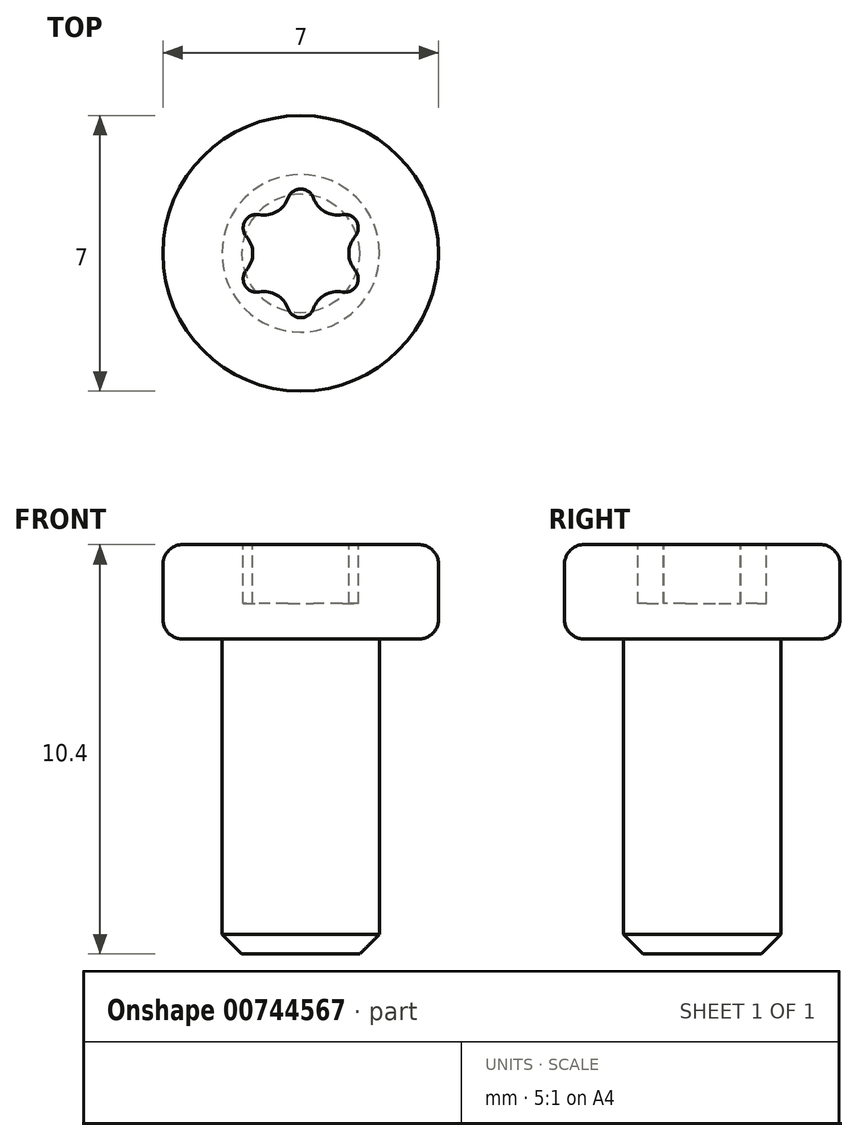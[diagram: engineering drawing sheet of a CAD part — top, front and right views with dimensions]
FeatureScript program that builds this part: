
annotation { "Feature Type Name" : "Feature", "Feature Type Description" : "" }
export const myFeature = defineFeature(function(context is Context, id is Id, definition is map)
    precondition{}
    {
        {
            var Q0;
            Q0=qCreatedBy(makeId("Top.planeOp"),FACE);
            var sketch = newSketch(context, id + "F0", { "sketchPlane" : qUnion([Q0])});
            skCircle(sketch, "E0", {"center": v(0, 0) * mm, "radius": 2 * mm});
            skSolve(sketch);
        }
        {
            var Q0;
            Q0=makeQuery(id+"F0.imprint","IMPRINT",FACE,{"disambiguationData":[TD([[makeQuery(id+"F0.imprint","IMPRINT",EDGE,{"derivedFrom":sQuery(id+"F0.wireOp",EDGE,"E0")}),1.0]])]});
            extrude(context, id + "F1", {"entities" : qUnion([Q0]), "depth" : 8 * mm, "offsetDistance" : 25 * mm});
        }
        {
            var Q0;
            Q0=makeQuery(id+"F1.opExtrude","CAP_FACE",FACE,{"disambiguationData":[OSD([sQuery(id+"F0.wireOp",EDGE,"E0")])],"isStart":false});
            var sketch = newSketch(context, id + "F2", { "sketchPlane" : qUnion([Q0])});
            skCircle(sketch, "E1", {"center": v(0, 0) * mm, "radius": 3.5 * mm});
            skSolve(sketch);
        }
        {
            var Q0;
            Q0 = qSketchRegion(id + "F2", true);
            extrude(context, id + "F3", {"entities" : qUnion([Q0]), "operationType" : NewBodyOperationType.ADD, "depth" : 2.4 * mm, "offsetDistance" : 25 * mm});
        }
        {
            var Q0;
            Q0=makeQuery(id+"F3.opExtrude","CAP_EDGE",EDGE,{"disambiguationData":[OSD([sQuery(id+"F2.wireOp",EDGE,"E1")])],"isStart":false});
            var Q1;
            Q1=makeQuery(id+"F3.opExtrude","CAP_EDGE",EDGE,{"disambiguationData":[OSD([sQuery(id+"F2.wireOp",EDGE,"E1")])],"isStart":true});
            fillet(context, id + "F4", {"entities" : qUnion([Q0, Q1]), "radius" : 0.5 * mm, "tangentPropagation" : true, "allowEdgeOverflow" : false});
        }
        {
            var Q0;
            Q0=makeQuery(id+"F1.opExtrude","CAP_EDGE",EDGE,{"disambiguationData":[OSD([sQuery(id+"F0.wireOp",EDGE,"E0")])],"isStart":true});
            chamfer(context, id + "F5", {"entities" : qUnion([Q0]), "width" : 0.5 * mm, "tangentPropagation" : true});
        }
        {
            var Q0;
            Q0=makeQuery(id+"F3.opExtrude","CAP_FACE",FACE,{"disambiguationData":[OSD([sQuery(id+"F2.wireOp",EDGE,"E1")])],"isStart":false});
            var sketch = newSketch(context, id + "F6", { "sketchPlane" : qUnion([Q0])});
            skCircle(sketch, "E2", {"center": v(0, 0) * mm, "radius": 1.64 * mm, "construction": true});
            skCircle(sketch, "E3", {"center": v(0, 0) * mm, "radius": 1.22 * mm, "construction": true});
            skLineSegment(sketch, "E4", {"start": v(0, 0) * mm, "end": v(0, 3.83) * mm, "construction": true});
            skLineSegment(sketch, "E5", {"start": v(0, 0) * mm, "end": v(2.44, 0) * mm, "construction": true});
            skArc(sketch, "E6", {"start": v(0.32, 1.4) * mm, "mid": v(0, 1.64) * mm, "end": v(-0.32, 1.4) * mm});
            skArc(sketch, "E7.1.0", {"start": v(-1.06, 0.98) * mm, "mid": v(-1.42, 0.82) * mm, "end": v(-1.38, 0.43) * mm});
            skLineSegment(sketch, "E7.1.1", {"start": v(0, 0) * mm, "end": v(1.22, 2.11) * mm, "construction": true});
            skLineSegment(sketch, "E7.2.1", {"start": v(0, 0) * mm, "end": v(-1.22, 2.11) * mm, "construction": true});
            skLineSegment(sketch, "E7.3.1", {"start": v(0, 0) * mm, "end": v(-2.44, 0) * mm, "construction": true});
            skLineSegment(sketch, "E7.4.1", {"start": v(0, 0) * mm, "end": v(-1.22, -2.11) * mm, "construction": true});
            skLineSegment(sketch, "E7.5.1", {"start": v(0, 0) * mm, "end": v(1.22, -2.11) * mm, "construction": true});
            skArc(sketch, "E8", {"start": v(0.32, 1.4) * mm, "mid": v(0.7, 1.01) * mm, "end": v(1.25, 1.05) * mm});
            skArc(sketch, "E9.1.0", {"start": v(-1.06, 0.98) * mm, "mid": v(-0.61, 1.06) * mm, "end": v(-0.32, 1.4) * mm});
            skArc(sketch, "E9.2.0", {"start": v(-1.54, -0.56) * mm, "mid": v(-1.23, -0.1) * mm, "end": v(-1.38, 0.43) * mm});
            skArc(sketch, "E9.3.0", {"start": v(-0.29, -1.6) * mm, "mid": v(-0.61, -1.06) * mm, "end": v(-1.25, -1.05) * mm});
            skArc(sketch, "E9.4.0", {"start": v(1.25, -1.05) * mm, "mid": v(0.61, -1.06) * mm, "end": v(0.29, -1.6) * mm});
            skArc(sketch, "E9.5.0", {"start": v(1.54, 0.56) * mm, "mid": v(1.22, 0) * mm, "end": v(1.54, -0.56) * mm});
            skArc(sketch, "E10.trimOffspring", {"start": v(1.38, 0.43) * mm, "mid": v(1.42, 0.82) * mm, "end": v(1.06, 0.98) * mm});
            skArc(sketch, "E11.trimOffspring", {"start": v(1.06, -0.98) * mm, "mid": v(1.42, -0.82) * mm, "end": v(1.38, -0.43) * mm});
            skArc(sketch, "E12.trimOffspring", {"start": v(-0.32, -1.4) * mm, "mid": v(0, -1.64) * mm, "end": v(0.32, -1.4) * mm});
            skArc(sketch, "E13.trimOffspring", {"start": v(-1.38, -0.43) * mm, "mid": v(-1.42, -0.82) * mm, "end": v(-1.06, -0.98) * mm});
            skSolve(sketch);
        }
        {
            var Q0;
            {var subQ9=sQuery(id+"F6.wireOp",EDGE,"E6");Q0=makeQuery(id+"F6.imprint","IMPRINT",FACE,{"disambiguationData":[TD([[makeQuery(id+"F6.imprint","IMPRINT",EDGE,{"derivedFrom":subQ9}),1.0]])]});}
            extrude(context, id + "F7", {"entities" : qUnion([Q0]), "operationType" : NewBodyOperationType.REMOVE, "oppositeDirection" : true, "depth" : 1.5 * mm, "offsetDistance" : 25 * mm});
        }
    });
